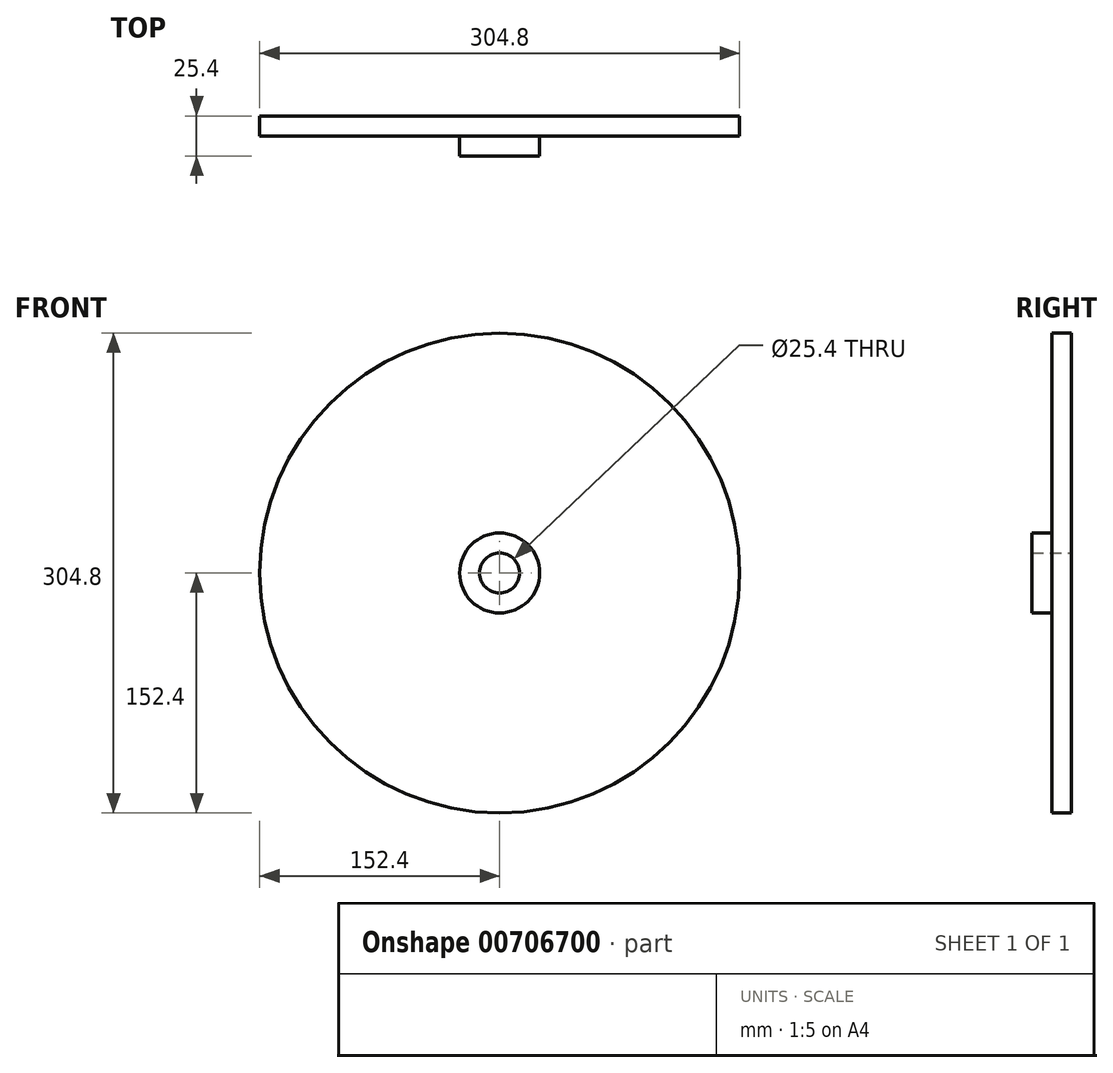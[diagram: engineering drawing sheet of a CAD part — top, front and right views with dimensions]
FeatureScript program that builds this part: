
annotation { "Feature Type Name" : "Feature", "Feature Type Description" : "" }
export const myFeature = defineFeature(function(context is Context, id is Id, definition is map)
    precondition{}
    {
        {
            var Q0;
            Q0=qCreatedBy(makeId("Front.planeOp"),FACE);
            var sketch = newSketch(context, id + "F0", { "sketchPlane" : qUnion([Q0])});
            skCircle(sketch, "E0", {"center": v(0, 0) * mm, "radius": 152.4 * mm});
            skSolve(sketch);
        }
        {
            var Q0;
            Q0=makeQuery(id+"F0.imprint","IMPRINT",FACE,{"disambiguationData":[TD([[makeQuery(id+"F0.imprint","IMPRINT",EDGE,{"derivedFrom":sQuery(id+"F0.wireOp",EDGE,"E0")}),1.0]])]});
            extrude(context, id + "F1", {"entities" : qUnion([Q0]), "depth" : 12.7 * mm, "offsetDistance" : 25.4 * mm});
        }
        {
            var Q0;
            Q0=makeQuery(id+"F1.opExtrude","CAP_FACE",FACE,{"disambiguationData":[OSD([sQuery(id+"F0.wireOp",EDGE,"E0")])],"isStart":false});
            var sketch = newSketch(context, id + "F2", { "sketchPlane" : qUnion([Q0])});
            skCircle(sketch, "E1", {"center": v(0, 0) * mm, "radius": 25.4 * mm});
            skSolve(sketch);
        }
        {
            var Q0;
            Q0=makeQuery(id+"F2.imprint","IMPRINT",FACE,{"disambiguationData":[TD([[makeQuery(id+"F2.imprint","IMPRINT",EDGE,{"derivedFrom":sQuery(id+"F2.wireOp",EDGE,"E1")}),1.0]])]});
            extrude(context, id + "F3", {"entities" : qUnion([Q0]), "operationType" : NewBodyOperationType.ADD, "depth" : 12.7 * mm, "offsetDistance" : 25.4 * mm});
        }
        {
            var Q0;
            Q0=makeQuery(id+"F1.opExtrude","CAP_FACE",FACE,{"disambiguationData":[OSD([sQuery(id+"F0.wireOp",EDGE,"E0")])],"isStart":true});
            var sketch = newSketch(context, id + "F4", { "sketchPlane" : qUnion([Q0])});
            skCircle(sketch, "E2", {"center": v(0, 0) * mm, "radius": 12.7 * mm});
            skSolve(sketch);
        }
        {
            var Q0;
            Q0=makeQuery(id+"F4.imprint","IMPRINT",FACE,{"disambiguationData":[TD([[makeQuery(id+"F4.imprint","IMPRINT",EDGE,{"derivedFrom":sQuery(id+"F4.wireOp",EDGE,"E2")}),1.0]])]});
            extrude(context, id + "F5", {"entities" : qUnion([Q0]), "operationType" : NewBodyOperationType.REMOVE, "oppositeDirection" : true, "depth" : 25.4 * mm, "offsetDistance" : 25.4 * mm});
        }
    });
